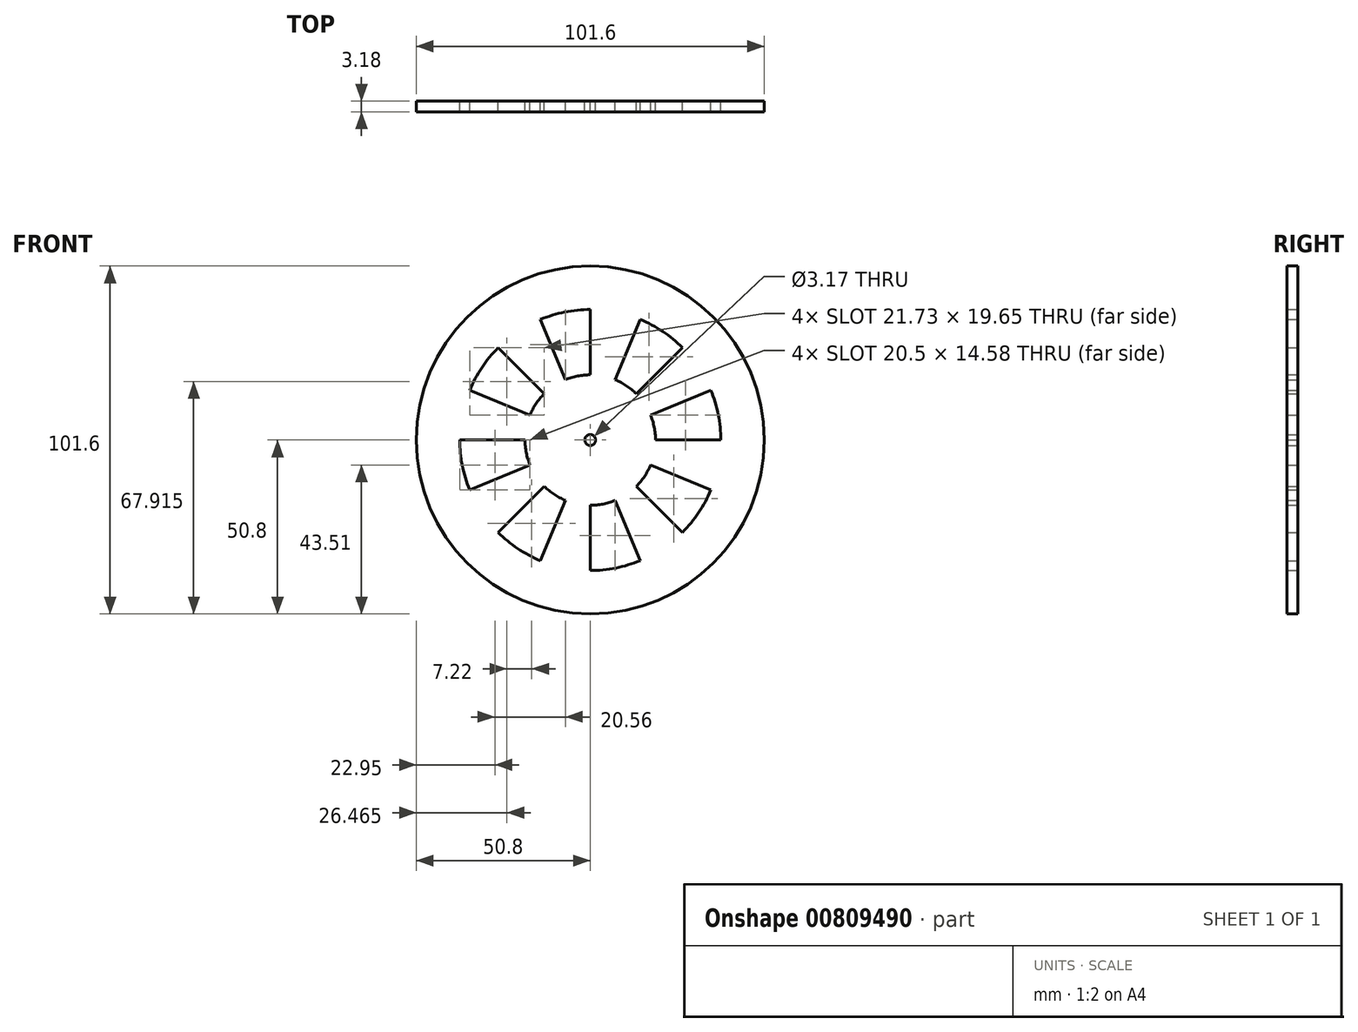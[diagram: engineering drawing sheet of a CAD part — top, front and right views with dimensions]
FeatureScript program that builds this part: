
annotation { "Feature Type Name" : "Feature", "Feature Type Description" : "" }
export const myFeature = defineFeature(function(context is Context, id is Id, definition is map)
    precondition{}
    {
        {
            var Q0;
            Q0=qCreatedBy(makeId("Front.planeOp"),FACE);
            var sketch = newSketch(context, id + "F0", { "sketchPlane" : qUnion([Q0])});
            skCircle(sketch, "E0", {"center": v(0, 0) * mm, "radius": 50.8 * mm});
            skCircle(sketch, "E1", {"center": v(0, 0) * mm, "radius": 19.05 * mm});
            skLineSegment(sketch, "E2", {"start": v(0, 50.8) * mm, "end": v(0, -50.8) * mm});
            skLineSegment(sketch, "E3", {"start": v(-50.8, 0) * mm, "end": v(50.8, 0) * mm});
            skLineSegment(sketch, "E4", {"start": v(35.92, 35.92) * mm, "end": v(0, 0) * mm});
            skLineSegment(sketch, "E5", {"start": v(0, 0) * mm, "end": v(-35.92, -35.92) * mm});
            skLineSegment(sketch, "E6", {"start": v(0, 0) * mm, "end": v(-35.92, 35.92) * mm});
            skLineSegment(sketch, "E7", {"start": v(0, 0) * mm, "end": v(35.92, -35.92) * mm});
            skLineSegment(sketch, "E8", {"start": v(-19.44, 46.93) * mm, "end": v(0, 0) * mm});
            skLineSegment(sketch, "E9", {"start": v(19.44, -46.93) * mm, "end": v(0, 0) * mm});
            skLineSegment(sketch, "E10", {"start": v(46.93, -19.44) * mm, "end": v(0, 0) * mm});
            skLineSegment(sketch, "E11", {"start": v(46.93, 19.44) * mm, "end": v(0, 0) * mm});
            skLineSegment(sketch, "E12", {"start": v(19.44, 46.93) * mm, "end": v(0, 0) * mm});
            skLineSegment(sketch, "E13", {"start": v(-46.93, 19.44) * mm, "end": v(0, 0) * mm});
            skLineSegment(sketch, "E14", {"start": v(-46.93, -19.44) * mm, "end": v(0, 0) * mm});
            skLineSegment(sketch, "E15", {"start": v(-19.44, -46.93) * mm, "end": v(0, 0) * mm});
            skCircle(sketch, "E16", {"center": v(0, 0) * mm, "radius": 38.1 * mm});
            skCircle(sketch, "E17", {"center": v(0, 0) * mm, "radius": 1.59 * mm});
            skSolve(sketch);
        }
        {
            var Q0;
            {var subQ0=sQuery(id+"F0.wireOp",EDGE,"E4");var subQ1=sQuery(id+"F0.wireOp",EDGE,"E0");var subQ2=makeQuery(id+"F0.imprint","INTERSECT",VERTEX,{"derivedFrom":[subQ1,subQ0]});Q0=makeQuery(id+"F0.imprint","IMPRINT",FACE,{"disambiguationData":[TD([[makeQuery(id+"F0.imprint","IMPRINT",EDGE,{"disambiguationData":[TD([[subQ2,-1.0]])],"derivedFrom":subQ1}),1.0]])]});}
            var Q1;
            {var subQ0=sQuery(id+"F0.wireOp",EDGE,"E2");var subQ1=sQuery(id+"F0.wireOp",EDGE,"E0");var subQ2=makeQuery(id+"F0.imprint","INTERSECT",VERTEX,{"disambiguationData":[OD(0.0)],"derivedFrom":[subQ1,subQ0]});Q1=makeQuery(id+"F0.imprint","IMPRINT",FACE,{"disambiguationData":[TD([[makeQuery(id+"F0.imprint","IMPRINT",EDGE,{"disambiguationData":[TD([[subQ2,-1.0]])],"derivedFrom":subQ1}),1.0]])]});}
            var Q2;
            {var subQ0=sQuery(id+"F0.wireOp",EDGE,"E6");var subQ1=sQuery(id+"F0.wireOp",EDGE,"E0");var subQ2=makeQuery(id+"F0.imprint","INTERSECT",VERTEX,{"derivedFrom":[subQ1,subQ0]});Q2=makeQuery(id+"F0.imprint","IMPRINT",FACE,{"disambiguationData":[TD([[makeQuery(id+"F0.imprint","IMPRINT",EDGE,{"disambiguationData":[TD([[subQ2,-1.0]])],"derivedFrom":subQ1}),1.0]])]});}
            var Q3;
            {var subQ0=sQuery(id+"F0.wireOp",EDGE,"E3");var subQ1=sQuery(id+"F0.wireOp",EDGE,"E0");var subQ2=makeQuery(id+"F0.imprint","INTERSECT",VERTEX,{"disambiguationData":[OD(0.0)],"derivedFrom":[subQ1,subQ0]});Q3=makeQuery(id+"F0.imprint","IMPRINT",FACE,{"disambiguationData":[TD([[makeQuery(id+"F0.imprint","IMPRINT",EDGE,{"disambiguationData":[TD([[subQ2,-1.0]])],"derivedFrom":subQ1}),1.0]])]});}
            var Q4;
            {var subQ0=sQuery(id+"F0.wireOp",EDGE,"E5");var subQ1=sQuery(id+"F0.wireOp",EDGE,"E0");var subQ2=makeQuery(id+"F0.imprint","INTERSECT",VERTEX,{"derivedFrom":[subQ1,subQ0]});Q4=makeQuery(id+"F0.imprint","IMPRINT",FACE,{"disambiguationData":[TD([[makeQuery(id+"F0.imprint","IMPRINT",EDGE,{"disambiguationData":[TD([[subQ2,-1.0]])],"derivedFrom":subQ1}),1.0]])]});}
            var Q5;
            {var subQ0=sQuery(id+"F0.wireOp",EDGE,"E2");var subQ1=sQuery(id+"F0.wireOp",EDGE,"E0");var subQ2=makeQuery(id+"F0.imprint","INTERSECT",VERTEX,{"disambiguationData":[OD(1.0)],"derivedFrom":[subQ1,subQ0]});Q5=makeQuery(id+"F0.imprint","IMPRINT",FACE,{"disambiguationData":[TD([[makeQuery(id+"F0.imprint","IMPRINT",EDGE,{"disambiguationData":[TD([[subQ2,-1.0]])],"derivedFrom":subQ1}),1.0]])]});}
            var Q6;
            {var subQ0=sQuery(id+"F0.wireOp",EDGE,"E7");var subQ1=sQuery(id+"F0.wireOp",EDGE,"E0");var subQ2=makeQuery(id+"F0.imprint","INTERSECT",VERTEX,{"derivedFrom":[subQ1,subQ0]});Q6=makeQuery(id+"F0.imprint","IMPRINT",FACE,{"disambiguationData":[TD([[makeQuery(id+"F0.imprint","IMPRINT",EDGE,{"disambiguationData":[TD([[subQ2,-1.0]])],"derivedFrom":subQ1}),1.0]])]});}
            var Q7;
            {var subQ0=sQuery(id+"F0.wireOp",EDGE,"E8");var subQ1=sQuery(id+"F0.wireOp",EDGE,"E1");var subQ2=makeQuery(id+"F0.imprint","INTERSECT",VERTEX,{"derivedFrom":[subQ1,subQ0]});Q7=makeQuery(id+"F0.imprint","IMPRINT",FACE,{"disambiguationData":[TD([[makeQuery(id+"F0.imprint","IMPRINT",EDGE,{"disambiguationData":[TD([[subQ2,-1.0]])],"derivedFrom":subQ1}),1.0]])]});}
            var Q8;
            {var subQ0=sQuery(id+"F0.wireOp",EDGE,"E12");var subQ1=sQuery(id+"F0.wireOp",EDGE,"E1");var subQ2=makeQuery(id+"F0.imprint","INTERSECT",VERTEX,{"derivedFrom":[subQ1,subQ0]});Q8=makeQuery(id+"F0.imprint","IMPRINT",FACE,{"disambiguationData":[TD([[makeQuery(id+"F0.imprint","IMPRINT",EDGE,{"disambiguationData":[TD([[subQ2,-1.0]])],"derivedFrom":subQ1}),1.0]])]});}
            var Q9;
            {var subQ0=sQuery(id+"F0.wireOp",EDGE,"E4");var subQ1=sQuery(id+"F0.wireOp",EDGE,"E1");var subQ2=makeQuery(id+"F0.imprint","INTERSECT",VERTEX,{"derivedFrom":[subQ1,subQ0]});Q9=makeQuery(id+"F0.imprint","IMPRINT",FACE,{"disambiguationData":[TD([[makeQuery(id+"F0.imprint","IMPRINT",EDGE,{"disambiguationData":[TD([[subQ2,-1.0]])],"derivedFrom":subQ1}),1.0]])]});}
            var Q10;
            {var subQ0=sQuery(id+"F0.wireOp",EDGE,"E11");var subQ1=sQuery(id+"F0.wireOp",EDGE,"E1");var subQ2=makeQuery(id+"F0.imprint","INTERSECT",VERTEX,{"derivedFrom":[subQ1,subQ0]});Q10=makeQuery(id+"F0.imprint","IMPRINT",FACE,{"disambiguationData":[TD([[makeQuery(id+"F0.imprint","IMPRINT",EDGE,{"disambiguationData":[TD([[subQ2,-1.0]])],"derivedFrom":subQ1}),1.0]])]});}
            var Q11;
            {var subQ0=sQuery(id+"F0.wireOp",EDGE,"E11");var subQ1=sQuery(id+"F0.wireOp",EDGE,"E1");var subQ2=makeQuery(id+"F0.imprint","INTERSECT",VERTEX,{"derivedFrom":[subQ1,subQ0]});Q11=makeQuery(id+"F0.imprint","IMPRINT",FACE,{"disambiguationData":[TD([[makeQuery(id+"F0.imprint","IMPRINT",EDGE,{"disambiguationData":[TD([[subQ2,1.0]])],"derivedFrom":subQ1}),1.0]])]});}
            var Q12;
            {var subQ0=sQuery(id+"F0.wireOp",EDGE,"E3");var subQ1=sQuery(id+"F0.wireOp",EDGE,"E1");var subQ2=makeQuery(id+"F0.imprint","INTERSECT",VERTEX,{"disambiguationData":[OD(0.0)],"derivedFrom":[subQ1,subQ0]});Q12=makeQuery(id+"F0.imprint","IMPRINT",FACE,{"disambiguationData":[TD([[makeQuery(id+"F0.imprint","IMPRINT",EDGE,{"disambiguationData":[TD([[subQ2,1.0]])],"derivedFrom":subQ1}),1.0]])]});}
            var Q13;
            {var subQ0=sQuery(id+"F0.wireOp",EDGE,"E9");var subQ1=sQuery(id+"F0.wireOp",EDGE,"E1");var subQ2=makeQuery(id+"F0.imprint","INTERSECT",VERTEX,{"derivedFrom":[subQ1,subQ0]});Q13=makeQuery(id+"F0.imprint","IMPRINT",FACE,{"disambiguationData":[TD([[makeQuery(id+"F0.imprint","IMPRINT",EDGE,{"disambiguationData":[TD([[subQ2,-1.0]])],"derivedFrom":subQ1}),1.0]])]});}
            var Q14;
            {var subQ0=sQuery(id+"F0.wireOp",EDGE,"E14");var subQ1=sQuery(id+"F0.wireOp",EDGE,"E1");var subQ2=makeQuery(id+"F0.imprint","INTERSECT",VERTEX,{"derivedFrom":[subQ1,subQ0]});Q14=makeQuery(id+"F0.imprint","IMPRINT",FACE,{"disambiguationData":[TD([[makeQuery(id+"F0.imprint","IMPRINT",EDGE,{"disambiguationData":[TD([[subQ2,-1.0]])],"derivedFrom":subQ1}),1.0]])]});}
            var Q15;
            {var subQ0=sQuery(id+"F0.wireOp",EDGE,"E13");var subQ1=sQuery(id+"F0.wireOp",EDGE,"E1");var subQ2=makeQuery(id+"F0.imprint","INTERSECT",VERTEX,{"derivedFrom":[subQ1,subQ0]});Q15=makeQuery(id+"F0.imprint","IMPRINT",FACE,{"disambiguationData":[TD([[makeQuery(id+"F0.imprint","IMPRINT",EDGE,{"disambiguationData":[TD([[subQ2,-1.0]])],"derivedFrom":subQ1}),1.0]])]});}
            var Q16;
            {var subQ0=sQuery(id+"F0.wireOp",EDGE,"E6");var subQ1=sQuery(id+"F0.wireOp",EDGE,"E1");var subQ2=makeQuery(id+"F0.imprint","INTERSECT",VERTEX,{"derivedFrom":[subQ1,subQ0]});Q16=makeQuery(id+"F0.imprint","IMPRINT",FACE,{"disambiguationData":[TD([[makeQuery(id+"F0.imprint","IMPRINT",EDGE,{"disambiguationData":[TD([[subQ2,-1.0]])],"derivedFrom":subQ1}),1.0]])]});}
            var Q17;
            {var subQ0=sQuery(id+"F0.wireOp",EDGE,"E3");var subQ1=sQuery(id+"F0.wireOp",EDGE,"E1");var subQ2=makeQuery(id+"F0.imprint","INTERSECT",VERTEX,{"disambiguationData":[OD(1.0)],"derivedFrom":[subQ1,subQ0]});Q17=makeQuery(id+"F0.imprint","IMPRINT",FACE,{"disambiguationData":[TD([[makeQuery(id+"F0.imprint","IMPRINT",EDGE,{"disambiguationData":[TD([[subQ2,-1.0]])],"derivedFrom":subQ1}),1.0]])]});}
            var Q18;
            {var subQ0=sQuery(id+"F0.wireOp",EDGE,"E5");var subQ1=sQuery(id+"F0.wireOp",EDGE,"E1");var subQ2=makeQuery(id+"F0.imprint","INTERSECT",VERTEX,{"derivedFrom":[subQ1,subQ0]});Q18=makeQuery(id+"F0.imprint","IMPRINT",FACE,{"disambiguationData":[TD([[makeQuery(id+"F0.imprint","IMPRINT",EDGE,{"disambiguationData":[TD([[subQ2,-1.0]])],"derivedFrom":subQ1}),1.0]])]});}
            var Q19;
            {var subQ0=sQuery(id+"F0.wireOp",EDGE,"E15");var subQ1=sQuery(id+"F0.wireOp",EDGE,"E1");var subQ2=makeQuery(id+"F0.imprint","INTERSECT",VERTEX,{"derivedFrom":[subQ1,subQ0]});Q19=makeQuery(id+"F0.imprint","IMPRINT",FACE,{"disambiguationData":[TD([[makeQuery(id+"F0.imprint","IMPRINT",EDGE,{"disambiguationData":[TD([[subQ2,-1.0]])],"derivedFrom":subQ1}),1.0]])]});}
            var Q20;
            {var subQ0=sQuery(id+"F0.wireOp",EDGE,"E2");var subQ1=sQuery(id+"F0.wireOp",EDGE,"E1");var subQ2=makeQuery(id+"F0.imprint","INTERSECT",VERTEX,{"disambiguationData":[OD(1.0)],"derivedFrom":[subQ1,subQ0]});Q20=makeQuery(id+"F0.imprint","IMPRINT",FACE,{"disambiguationData":[TD([[makeQuery(id+"F0.imprint","IMPRINT",EDGE,{"disambiguationData":[TD([[subQ2,-1.0]])],"derivedFrom":subQ1}),1.0]])]});}
            var Q21;
            {var subQ0=sQuery(id+"F0.wireOp",EDGE,"E7");var subQ1=sQuery(id+"F0.wireOp",EDGE,"E1");var subQ2=makeQuery(id+"F0.imprint","INTERSECT",VERTEX,{"derivedFrom":[subQ1,subQ0]});Q21=makeQuery(id+"F0.imprint","IMPRINT",FACE,{"disambiguationData":[TD([[makeQuery(id+"F0.imprint","IMPRINT",EDGE,{"disambiguationData":[TD([[subQ2,-1.0]])],"derivedFrom":subQ1}),1.0]])]});}
            var Q22;
            {var subQ0=sQuery(id+"F0.wireOp",EDGE,"E2");var subQ1=sQuery(id+"F0.wireOp",EDGE,"E1");var subQ2=makeQuery(id+"F0.imprint","INTERSECT",VERTEX,{"disambiguationData":[OD(0.0)],"derivedFrom":[subQ1,subQ0]});Q22=makeQuery(id+"F0.imprint","IMPRINT",FACE,{"disambiguationData":[TD([[makeQuery(id+"F0.imprint","IMPRINT",EDGE,{"disambiguationData":[TD([[subQ2,-1.0]])],"derivedFrom":subQ1}),1.0]])]});}
            var Q23;
            {var subQ0=sQuery(id+"F0.wireOp",EDGE,"E3");var subQ1=sQuery(id+"F0.wireOp",EDGE,"E0");var subQ2=makeQuery(id+"F0.imprint","INTERSECT",VERTEX,{"disambiguationData":[OD(1.0)],"derivedFrom":[subQ1,subQ0]});Q23=makeQuery(id+"F0.imprint","IMPRINT",FACE,{"disambiguationData":[TD([[makeQuery(id+"F0.imprint","IMPRINT",EDGE,{"disambiguationData":[TD([[subQ2,-1.0]])],"derivedFrom":subQ1}),1.0]])]});}
            var Q24;
            {var subQ0=sQuery(id+"F0.wireOp",EDGE,"E6");var subQ1=sQuery(id+"F0.wireOp",EDGE,"E0");var subQ2=makeQuery(id+"F0.imprint","INTERSECT",VERTEX,{"derivedFrom":[subQ1,subQ0]});Q24=makeQuery(id+"F0.imprint","IMPRINT",FACE,{"disambiguationData":[TD([[makeQuery(id+"F0.imprint","IMPRINT",EDGE,{"disambiguationData":[TD([[subQ2,1.0]])],"derivedFrom":subQ1}),1.0]])]});}
            var Q25;
            {var subQ0=sQuery(id+"F0.wireOp",EDGE,"E2");var subQ1=sQuery(id+"F0.wireOp",EDGE,"E0");var subQ2=makeQuery(id+"F0.imprint","INTERSECT",VERTEX,{"disambiguationData":[OD(0.0)],"derivedFrom":[subQ1,subQ0]});Q25=makeQuery(id+"F0.imprint","IMPRINT",FACE,{"disambiguationData":[TD([[makeQuery(id+"F0.imprint","IMPRINT",EDGE,{"disambiguationData":[TD([[subQ2,1.0]])],"derivedFrom":subQ1}),1.0]])]});}
            var Q26;
            {var subQ0=sQuery(id+"F0.wireOp",EDGE,"E4");var subQ1=sQuery(id+"F0.wireOp",EDGE,"E0");var subQ2=makeQuery(id+"F0.imprint","INTERSECT",VERTEX,{"derivedFrom":[subQ1,subQ0]});Q26=makeQuery(id+"F0.imprint","IMPRINT",FACE,{"disambiguationData":[TD([[makeQuery(id+"F0.imprint","IMPRINT",EDGE,{"disambiguationData":[TD([[subQ2,1.0]])],"derivedFrom":subQ1}),1.0]])]});}
            var Q27;
            {var subQ0=sQuery(id+"F0.wireOp",EDGE,"E7");var subQ1=sQuery(id+"F0.wireOp",EDGE,"E0");var subQ2=makeQuery(id+"F0.imprint","INTERSECT",VERTEX,{"derivedFrom":[subQ1,subQ0]});Q27=makeQuery(id+"F0.imprint","IMPRINT",FACE,{"disambiguationData":[TD([[makeQuery(id+"F0.imprint","IMPRINT",EDGE,{"disambiguationData":[TD([[subQ2,1.0]])],"derivedFrom":subQ1}),1.0]])]});}
            var Q28;
            {var subQ0=sQuery(id+"F0.wireOp",EDGE,"E2");var subQ1=sQuery(id+"F0.wireOp",EDGE,"E0");var subQ2=makeQuery(id+"F0.imprint","INTERSECT",VERTEX,{"disambiguationData":[OD(1.0)],"derivedFrom":[subQ1,subQ0]});Q28=makeQuery(id+"F0.imprint","IMPRINT",FACE,{"disambiguationData":[TD([[makeQuery(id+"F0.imprint","IMPRINT",EDGE,{"disambiguationData":[TD([[subQ2,1.0]])],"derivedFrom":subQ1}),1.0]])]});}
            var Q29;
            {var subQ0=sQuery(id+"F0.wireOp",EDGE,"E5");var subQ1=sQuery(id+"F0.wireOp",EDGE,"E0");var subQ2=makeQuery(id+"F0.imprint","INTERSECT",VERTEX,{"derivedFrom":[subQ1,subQ0]});Q29=makeQuery(id+"F0.imprint","IMPRINT",FACE,{"disambiguationData":[TD([[makeQuery(id+"F0.imprint","IMPRINT",EDGE,{"disambiguationData":[TD([[subQ2,1.0]])],"derivedFrom":subQ1}),1.0]])]});}
            var Q30;
            {var subQ0=sQuery(id+"F0.wireOp",EDGE,"E3");var subQ1=sQuery(id+"F0.wireOp",EDGE,"E0");var subQ2=makeQuery(id+"F0.imprint","INTERSECT",VERTEX,{"disambiguationData":[OD(0.0)],"derivedFrom":[subQ1,subQ0]});Q30=makeQuery(id+"F0.imprint","IMPRINT",FACE,{"disambiguationData":[TD([[makeQuery(id+"F0.imprint","IMPRINT",EDGE,{"disambiguationData":[TD([[subQ2,1.0]])],"derivedFrom":subQ1}),1.0]])]});}
            var Q31;
            {var subQ0=sQuery(id+"F0.wireOp",EDGE,"E13");var subQ1=sQuery(id+"F0.wireOp",EDGE,"E1");var subQ2=makeQuery(id+"F0.imprint","INTERSECT",VERTEX,{"derivedFrom":[subQ1,subQ0]});Q31=makeQuery(id+"F0.imprint","IMPRINT",FACE,{"disambiguationData":[TD([[makeQuery(id+"F0.imprint","IMPRINT",EDGE,{"disambiguationData":[TD([[subQ2,-1.0]])],"derivedFrom":subQ1}),-1.0]])]});}
            var Q32;
            {var subQ0=sQuery(id+"F0.wireOp",EDGE,"E8");var subQ1=sQuery(id+"F0.wireOp",EDGE,"E1");var subQ2=makeQuery(id+"F0.imprint","INTERSECT",VERTEX,{"derivedFrom":[subQ1,subQ0]});Q32=makeQuery(id+"F0.imprint","IMPRINT",FACE,{"disambiguationData":[TD([[makeQuery(id+"F0.imprint","IMPRINT",EDGE,{"disambiguationData":[TD([[subQ2,-1.0]])],"derivedFrom":subQ1}),-1.0]])]});}
            var Q33;
            {var subQ0=sQuery(id+"F0.wireOp",EDGE,"E12");var subQ1=sQuery(id+"F0.wireOp",EDGE,"E1");var subQ2=makeQuery(id+"F0.imprint","INTERSECT",VERTEX,{"derivedFrom":[subQ1,subQ0]});Q33=makeQuery(id+"F0.imprint","IMPRINT",FACE,{"disambiguationData":[TD([[makeQuery(id+"F0.imprint","IMPRINT",EDGE,{"disambiguationData":[TD([[subQ2,-1.0]])],"derivedFrom":subQ1}),-1.0]])]});}
            var Q34;
            {var subQ0=sQuery(id+"F0.wireOp",EDGE,"E11");var subQ1=sQuery(id+"F0.wireOp",EDGE,"E1");var subQ2=makeQuery(id+"F0.imprint","INTERSECT",VERTEX,{"derivedFrom":[subQ1,subQ0]});Q34=makeQuery(id+"F0.imprint","IMPRINT",FACE,{"disambiguationData":[TD([[makeQuery(id+"F0.imprint","IMPRINT",EDGE,{"disambiguationData":[TD([[subQ2,-1.0]])],"derivedFrom":subQ1}),-1.0]])]});}
            var Q35;
            {var subQ0=sQuery(id+"F0.wireOp",EDGE,"E3");var subQ1=sQuery(id+"F0.wireOp",EDGE,"E1");var subQ2=makeQuery(id+"F0.imprint","INTERSECT",VERTEX,{"disambiguationData":[OD(0.0)],"derivedFrom":[subQ1,subQ0]});Q35=makeQuery(id+"F0.imprint","IMPRINT",FACE,{"disambiguationData":[TD([[makeQuery(id+"F0.imprint","IMPRINT",EDGE,{"disambiguationData":[TD([[subQ2,1.0]])],"derivedFrom":subQ1}),-1.0]])]});}
            var Q36;
            {var subQ0=sQuery(id+"F0.wireOp",EDGE,"E15");var subQ1=sQuery(id+"F0.wireOp",EDGE,"E1");var subQ2=makeQuery(id+"F0.imprint","INTERSECT",VERTEX,{"derivedFrom":[subQ1,subQ0]});Q36=makeQuery(id+"F0.imprint","IMPRINT",FACE,{"disambiguationData":[TD([[makeQuery(id+"F0.imprint","IMPRINT",EDGE,{"disambiguationData":[TD([[subQ2,-1.0]])],"derivedFrom":subQ1}),-1.0]])]});}
            var Q37;
            {var subQ0=sQuery(id+"F0.wireOp",EDGE,"E14");var subQ1=sQuery(id+"F0.wireOp",EDGE,"E1");var subQ2=makeQuery(id+"F0.imprint","INTERSECT",VERTEX,{"derivedFrom":[subQ1,subQ0]});Q37=makeQuery(id+"F0.imprint","IMPRINT",FACE,{"disambiguationData":[TD([[makeQuery(id+"F0.imprint","IMPRINT",EDGE,{"disambiguationData":[TD([[subQ2,-1.0]])],"derivedFrom":subQ1}),-1.0]])]});}
            var Q38;
            {var subQ0=sQuery(id+"F0.wireOp",EDGE,"E3");var subQ1=sQuery(id+"F0.wireOp",EDGE,"E0");var subQ2=makeQuery(id+"F0.imprint","INTERSECT",VERTEX,{"disambiguationData":[OD(1.0)],"derivedFrom":[subQ1,subQ0]});Q38=makeQuery(id+"F0.imprint","IMPRINT",FACE,{"disambiguationData":[TD([[makeQuery(id+"F0.imprint","IMPRINT",EDGE,{"disambiguationData":[TD([[subQ2,1.0]])],"derivedFrom":subQ1}),1.0]])]});}
            var Q39;
            {var subQ0=sQuery(id+"F0.wireOp",EDGE,"E9");var subQ1=sQuery(id+"F0.wireOp",EDGE,"E1");var subQ2=makeQuery(id+"F0.imprint","INTERSECT",VERTEX,{"derivedFrom":[subQ1,subQ0]});Q39=makeQuery(id+"F0.imprint","IMPRINT",FACE,{"disambiguationData":[TD([[makeQuery(id+"F0.imprint","IMPRINT",EDGE,{"disambiguationData":[TD([[subQ2,-1.0]])],"derivedFrom":subQ1}),-1.0]])]});}
            extrude(context, id + "F1", {"entities" : qUnion([Q0, Q1, Q2, Q3, Q4, Q5, Q6, Q7, Q8, Q9, Q10, Q11, Q12, Q13, Q14, Q15, Q16, Q17, Q18, Q19, Q20, Q21, Q22, Q23, Q24, Q25, Q26, Q27, Q28, Q29, Q30, Q31, Q32, Q33, Q34, Q35, Q36, Q37, Q38, Q39]), "depth" : 3.17 * mm, "offsetDistance" : 25.4 * mm});
        }
    });
